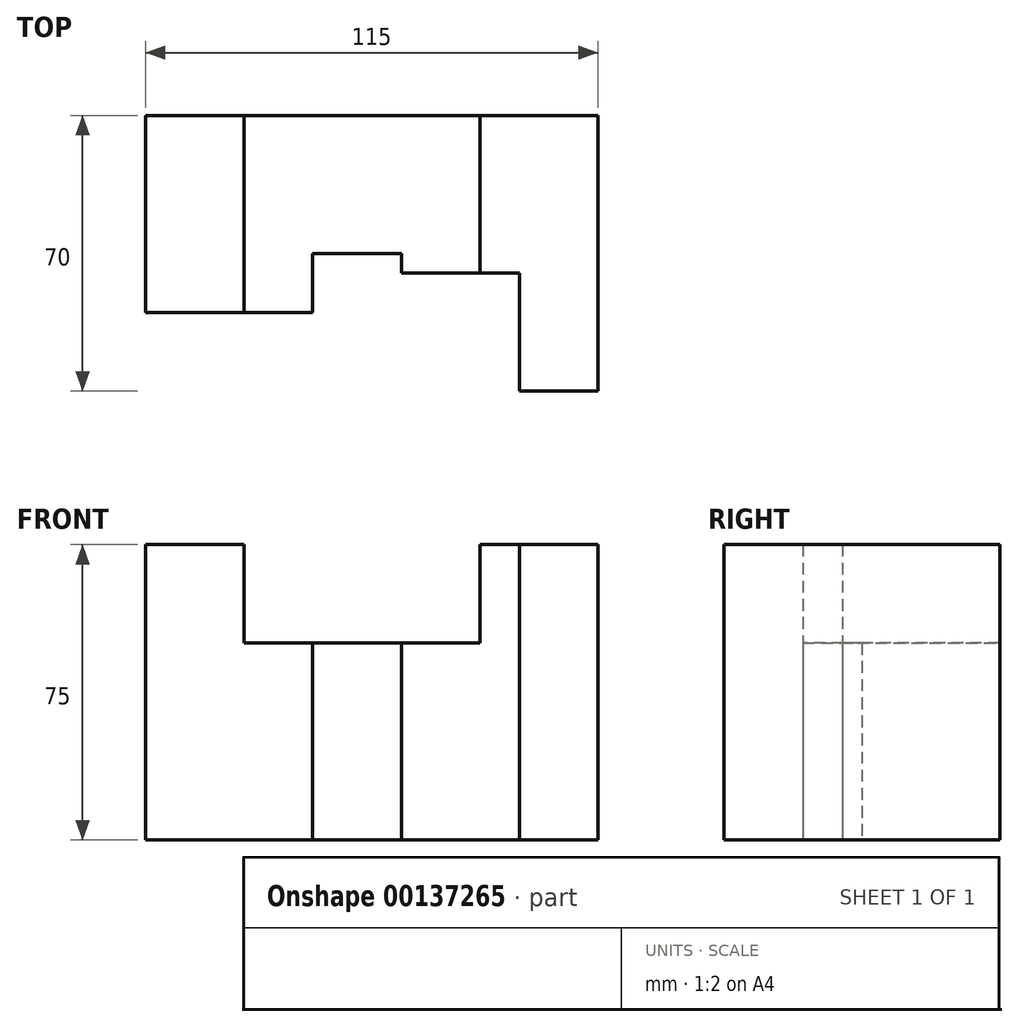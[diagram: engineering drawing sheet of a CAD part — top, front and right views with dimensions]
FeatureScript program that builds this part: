
annotation { "Feature Type Name" : "Feature", "Feature Type Description" : "" }
export const myFeature = defineFeature(function(context is Context, id is Id, definition is map)
    precondition{}
    {
        {
            var Q0;
            Q0=qCreatedBy(makeId("Top.planeOp"),FACE);
            var sketch = newSketch(context, id + "F0", { "sketchPlane" : qUnion([Q0])});
            skLineSegment(sketch, "E0.bottom", {"start": v(0, 0) * mm, "end": v(25, 0) * mm});
            skLineSegment(sketch, "E0.top", {"start": v(0, 50) * mm, "end": v(25, 50) * mm});
            skLineSegment(sketch, "E0.left", {"start": v(0, 0) * mm, "end": v(0, 50) * mm});
            skLineSegment(sketch, "E0.right", {"start": v(25, 0) * mm, "end": v(25, 50) * mm});
            skLineSegment(sketch, "E1", {"start": v(25, 50) * mm, "end": v(85, 50) * mm});
            skLineSegment(sketch, "E2", {"start": v(85, 50) * mm, "end": v(85, 10) * mm});
            skLineSegment(sketch, "E3", {"start": v(85, 10) * mm, "end": v(65, 10) * mm});
            skLineSegment(sketch, "E4", {"start": v(65, 10) * mm, "end": v(65, 15) * mm});
            skLineSegment(sketch, "E5", {"start": v(65, 15) * mm, "end": v(42.5, 15) * mm});
            skLineSegment(sketch, "E6", {"start": v(42.5, 15) * mm, "end": v(42.5, 0) * mm});
            skLineSegment(sketch, "E7", {"start": v(42.5, 0) * mm, "end": v(25, 0) * mm});
            skLineSegment(sketch, "E8", {"start": v(85, 10) * mm, "end": v(95, 10) * mm});
            skLineSegment(sketch, "E9", {"start": v(95, 10) * mm, "end": v(95, -20) * mm});
            skLineSegment(sketch, "E10", {"start": v(95, -20) * mm, "end": v(115, -20) * mm});
            skLineSegment(sketch, "E11", {"start": v(115, -20) * mm, "end": v(115, 50) * mm});
            skLineSegment(sketch, "E12", {"start": v(115, 50) * mm, "end": v(85, 50) * mm});
            skSolve(sketch);
        }
        {
            var Q0;
            Q0=makeQuery(id+"F0.imprint","IMPRINT",FACE,{"disambiguationData":[TD([[makeQuery(id+"F0.imprint","IMPRINT",EDGE,{"derivedFrom":sQuery(id+"F0.wireOp",EDGE,"E0.bottom")}),1.0]])]});
            extrude(context, id + "F1", {"entities" : qUnion([Q0]), "depth" : (15 * 5) * mm});
        }
        {
            var Q0;
            Q0=makeQuery(id+"F0.imprint","IMPRINT",FACE,{"disambiguationData":[TD([[makeQuery(id+"F0.imprint","IMPRINT",EDGE,{"derivedFrom":sQuery(id+"F0.wireOp",EDGE,"E0.right")}),-1.0]])]});
            extrude(context, id + "F2", {"entities" : qUnion([Q0]), "operationType" : NewBodyOperationType.ADD, "depth" : 50 * mm});
        }
        {
            var Q0;
            Q0=makeQuery(id+"F0.imprint","IMPRINT",FACE,{"disambiguationData":[TD([[makeQuery(id+"F0.imprint","IMPRINT",EDGE,{"derivedFrom":sQuery(id+"F0.wireOp",EDGE,"E2")}),1.0]])]});
            extrude(context, id + "F3", {"entities" : qUnion([Q0]), "operationType" : NewBodyOperationType.ADD, "depth" : (15 * 5) * mm});
        }
    });
